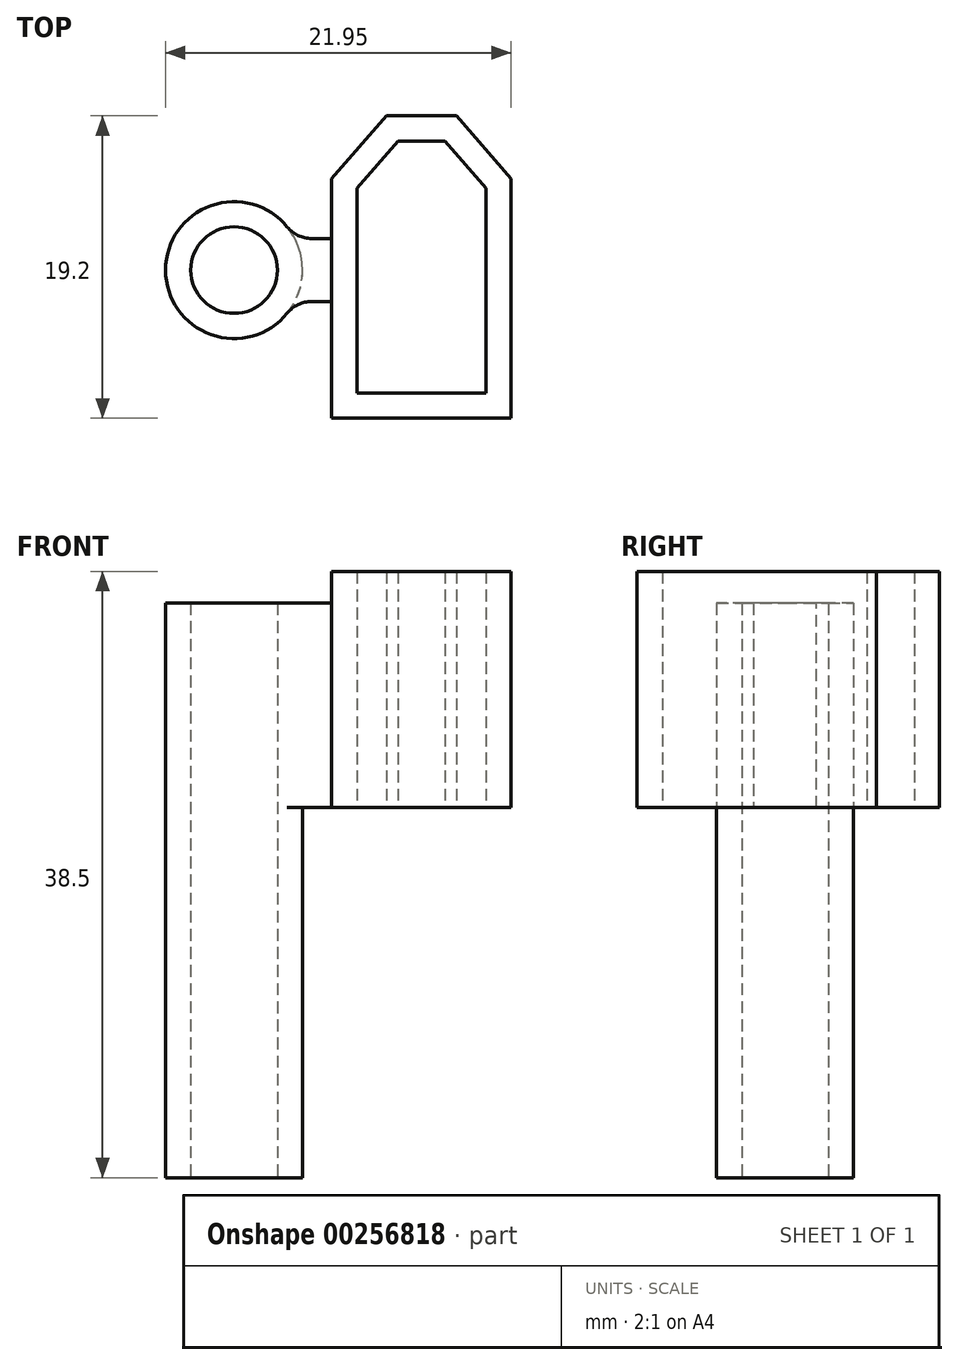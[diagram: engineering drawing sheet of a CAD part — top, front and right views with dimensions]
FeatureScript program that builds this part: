
annotation { "Feature Type Name" : "Feature", "Feature Type Description" : "" }
export const myFeature = defineFeature(function(context is Context, id is Id, definition is map)
    precondition{}
    {
        {
            var Q0;
            Q0=qCreatedBy(makeId("Top.planeOp"),FACE);
            var sketch = newSketch(context, id + "F0", { "sketchPlane" : qUnion([Q0])});
            skLineSegment(sketch, "E0", {"start": v(0, 8.2) * mm, "end": v(-1.5, 8.2) * mm});
            skLineSegment(sketch, "E1", {"start": v(-1.5, 8.2) * mm, "end": v(-4.1, 5.2) * mm});
            skLineSegment(sketch, "E2", {"start": v(-4.1, 5.2) * mm, "end": v(-4.1, -7.8) * mm});
            skLineSegment(sketch, "E3", {"start": v(-4.1, -7.8) * mm, "end": v(0, -7.8) * mm});
            skLineSegment(sketch, "E4.MirrorCS", {"start": v(4.1, -7.8) * mm, "end": v(0, -7.8) * mm});
            skLineSegment(sketch, "E5.MirrorCS", {"start": v(4.1, 5.2) * mm, "end": v(4.1, -7.8) * mm});
            skLineSegment(sketch, "E6.MirrorCS", {"start": v(0, 8.2) * mm, "end": v(1.5, 8.2) * mm});
            skLineSegment(sketch, "E7.MirrorCS", {"start": v(1.5, 8.2) * mm, "end": v(4.1, 5.2) * mm});
            skLineSegment(sketch, "E8.0", {"start": v(0, 9.8) * mm, "end": v(-2.23, 9.8) * mm});
            skLineSegment(sketch, "E8.1", {"start": v(0, 9.8) * mm, "end": v(2.23, 9.8) * mm});
            skLineSegment(sketch, "E8.2", {"start": v(-2.23, 9.8) * mm, "end": v(-5.7, 5.8) * mm});
            skLineSegment(sketch, "E8.3", {"start": v(2.23, 9.8) * mm, "end": v(5.7, 5.8) * mm});
            skLineSegment(sketch, "E8.4", {"start": v(-5.7, 5.8) * mm, "end": v(-5.7, -9.4) * mm});
            skLineSegment(sketch, "E8.5", {"start": v(-5.7, -9.4) * mm, "end": v(0, -9.4) * mm});
            skLineSegment(sketch, "E8.6", {"start": v(5.7, -9.4) * mm, "end": v(0, -9.4) * mm});
            skLineSegment(sketch, "E8.7", {"start": v(5.7, 5.8) * mm, "end": v(5.7, -9.4) * mm});
            skCircle(sketch, "E9", {"center": v(-11.9, 0) * mm, "radius": 4.35 * mm});
            skCircle(sketch, "E10", {"center": v(-11.9, 0) * mm, "radius": 2.75 * mm});
            skLineSegment(sketch, "E11.bottom", {"start": v(-5.7, 2) * mm, "end": v(-8.4, 2) * mm});
            skLineSegment(sketch, "E11.top", {"start": v(-5.7, -2) * mm, "end": v(-8.4, -2) * mm});
            skLineSegment(sketch, "E11.left", {"start": v(-5.7, 2) * mm, "end": v(-5.7, -2) * mm});
            skLineSegment(sketch, "E11.right", {"start": v(-8.4, 2) * mm, "end": v(-8.4, -2) * mm});
            skSolve(sketch);
        }
        {
            var Q0;
            Q0=makeQuery(id+"F0.imprint","IMPRINT",FACE,{"disambiguationData":[TD([[makeQuery(id+"F0.imprint","IMPRINT",EDGE,{"derivedFrom":sQuery(id+"F0.wireOp",EDGE,"E0")}),-1.0]])]});
            extrude(context, id + "F1", {"entities" : qUnion([Q0]), "depth" : 15 * mm});
        }
        {
            var Q0;
            {var subQ5=sQuery(id+"F0.wireOp",EDGE,"E11.left");Q0=makeQuery(id+"F0.imprint","IMPRINT",FACE,{"disambiguationData":[TD([[makeQuery(id+"F0.imprint","IMPRINT",EDGE,{"derivedFrom":subQ5}),-1.0]])]});}
            var Q1;
            {var subQ0=sQuery(id+"F0.wireOp",EDGE,"E11.bottom");var subQ1=sQuery(id+"F0.wireOp",EDGE,"E8.4");var subQ2=makeQuery(id+"F0.imprint","INTERSECT",VERTEX,{"derivedFrom":[subQ1,subQ0]});Q1=makeQuery(id+"F0.imprint","IMPRINT",FACE,{"disambiguationData":[TD([[makeQuery(id+"F0.imprint","IMPRINT",EDGE,{"disambiguationData":[TD([[subQ2,-1.0]])],"derivedFrom":subQ1}),-1.0]])]});}
            var Q2;
            {var subQ5=sQuery(id+"F0.wireOp",EDGE,"E11.right");Q2=makeQuery(id+"F0.imprint","IMPRINT",FACE,{"disambiguationData":[TD([[makeQuery(id+"F0.imprint","IMPRINT",EDGE,{"derivedFrom":subQ5}),1.0]])]});}
            extrude(context, id + "F2", {"entities" : qUnion([Q0, Q1, Q2]), "operationType" : NewBodyOperationType.ADD, "depth" : 13 * mm});
        }
        {
            var Q0;
            Q0=makeQuery(id+"F0.imprint","IMPRINT",FACE,{"disambiguationData":[TD([[makeQuery(id+"F0.imprint","IMPRINT",EDGE,{"derivedFrom":sQuery(id+"F0.wireOp",EDGE,"E10")}),-1.0]])]});
            var Q1;
            {var subQ5=sQuery(id+"F0.wireOp",EDGE,"E11.right");Q1=makeQuery(id+"F0.imprint","IMPRINT",FACE,{"disambiguationData":[TD([[makeQuery(id+"F0.imprint","IMPRINT",EDGE,{"derivedFrom":subQ5}),1.0]])]});}
            extrude(context, id + "F3", {"entities" : qUnion([Q0, Q1]), "operationType" : NewBodyOperationType.ADD, "depth" : 13 * mm, "hasSecondDirection" : true, "secondDirectionOppositeDirection" : true, "secondDirectionDepth" : 23.5 * mm});
        }
        {
            var Q0;
            Q0=makeQuery(id+"F2.opExtrude","SWEPT_EDGE",EDGE,{"disambiguationData":[OSD([sQuery(id+"F0.wireOp",EDGE,"E8.4"),sQuery(id+"F0.wireOp",EDGE,"E11.top"),sQuery(id+"F0.wireOp",EDGE,"E11.left")])]});
            var Q1;
            Q1=makeQuery(id+"F3.boolean.opBoolean","INTERSECT",EDGE,{"derivedFrom":[makeQuery(id+"F2.opExtrude","SWEPT_FACE",FACE,{"disambiguationData":[OSD([sQuery(id+"F0.wireOp",EDGE,"E11.bottom")])]}),makeQuery(id+"F3.opExtrude","SWEPT_FACE",FACE,{"disambiguationData":[OSD([sQuery(id+"F0.wireOp",EDGE,"E9")])]})]});
            var Q2;
            Q2=makeQuery(id+"F2.opExtrude","SWEPT_EDGE",EDGE,{"disambiguationData":[OSD([sQuery(id+"F0.wireOp",EDGE,"E8.4"),sQuery(id+"F0.wireOp",EDGE,"E11.bottom"),sQuery(id+"F0.wireOp",EDGE,"E11.left")])]});
            var Q3;
            Q3=makeQuery(id+"F3.boolean.opBoolean","INTERSECT",EDGE,{"derivedFrom":[makeQuery(id+"F2.opExtrude","SWEPT_FACE",FACE,{"disambiguationData":[OSD([sQuery(id+"F0.wireOp",EDGE,"E11.top")])]}),makeQuery(id+"F3.opExtrude","SWEPT_FACE",FACE,{"disambiguationData":[OSD([sQuery(id+"F0.wireOp",EDGE,"E9")])]})]});
            fillet(context, id + "F4", {"entities" : qUnion([Q0, Q1, Q2, Q3]), "radius" : 2 * mm, "tangentPropagation" : true, "allowEdgeOverflow" : false});
        }
    });
